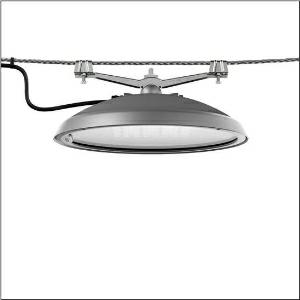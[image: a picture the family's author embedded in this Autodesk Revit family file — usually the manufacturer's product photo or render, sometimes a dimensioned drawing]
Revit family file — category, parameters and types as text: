
# Revit family: dl_r__50_iq_mini___st1_0s_5xa248w21f08re_f800
name_source: partatom
category: Lighting Fixtures
units: mm (PartAtom-declared; Revit-internal decimal feet)

## family parameters
Cut with Voids When Loaded = No
Host = Face
Light Source = No
Part Type = Normal
Room Calculation Point = No
Round Connector Dimension = Use Diameter
Shared = No

## types (1)
- --- (1 x LED, 5120 lm, 36.6 W, 2200K)
    Apparent Load = 37 VA
    CIE Flux Codes = 37 72 97 100 100
    Color Rendering = 70
    Color Temperature = 2200K
    Default Elevation = 1800 mm
    Description = DL® 50 iQ mini, catenary luminaire, primary light control with lens, of PMMA, primary optical cover: cover, of toughened safety glass, transparent, light distribution: ST1.0s, light emission: direct distribution, primary light characteristic: symmetric, installation type: suspended mounting, LED, High Power LED, rated luminous flux: 5.120lm, luminous efficacy: 140lm/W, light colour: 722, colour temperature: 2200K, control gear: iQ Street-Remote, control: optimised constant luminous flux control (CLO 2.0), Desk-Remote (wireless, voltage-free reading and setting of iQ features in the workshop via application-optimized NFC function/RFID function), Light-Fading, Smart-Wire, Night-Set, Lumen-Switch, Temp-Guard, Auto-Match, Street-Remote, mains connection: 230..240V, AC, 50/60Hz, start of lifetime: 37W, end of service life: 38W, reduction: 18W, luminaire housing, of diecast aluminium, powder-coated, Siteco® metallic grey (DB 702S), diameter: 500mm, height: 115mm, mounting height: 4..12m, protection rating (complete): IP66, insulation class (complete): insulation class II (safety insulation), certification: CE, ENEC, ENEC+, VDE, impact resistance: IK08, permissible operating ambient temperature for outdoor applications: -25..+40°C, standard-compliant lighting for roads and squares, packaging unit: 1 piece

Light Distribution: ST1.0s
    Height = 124 mm  [stored 0.406824 ft]
    Lamp = 1 x LED
    Lamp Light Flux = 5120 lm
    Lamp Power = 36.6 W
    Lamp count = 1
    Length = 500 mm
    Luminous efficacy = 140 lm/W
    Manufacturer = Siteco
    ModVariant = No
    Model = 5XA248W21F08RE
    Number of Poles = 1
    OnlyDefault = Yes
    Power Factor = 1
    Product Name = DL® 50 iQ mini | ST1.0s
    Product group = catenary luminaire
    ProductGroupID = 6300
    Protection Class = Protection class II
    Protection Degree = IP 66
    RLX_Detail_Level = 1
    RLX_Emergency_Light_Flux = 0 lm
    RLX_Emergency_Type = 0
    RLX_Emergency_Type_DB = No
    RlxData = <blob elided: 123945 chars, md5=8075774a>
    Socket = socket
    Standby Power = 0 W
    System Light Flux = 5120 lm
    System Power = 37 W
    Type Comments = factory setting: luminous flux: 100 % | dim-lin: 254 | 388 mA
    Type Image = l_1242791.jpg
    URL = http://relux.com
    VarID = @adj_162271
    Voltage = 0 V
    Weight = 0.00 kg
    Width = 0 mm  [stored 0 ft]

note: [stored X ft] marks values corroborated as IEEE doubles in the binary element streams (Revit-internal decimal feet)

## geometry (parser evidence)
native form markers: Blend x4, Sweep x12
no freeform markers — native parametric forms only
